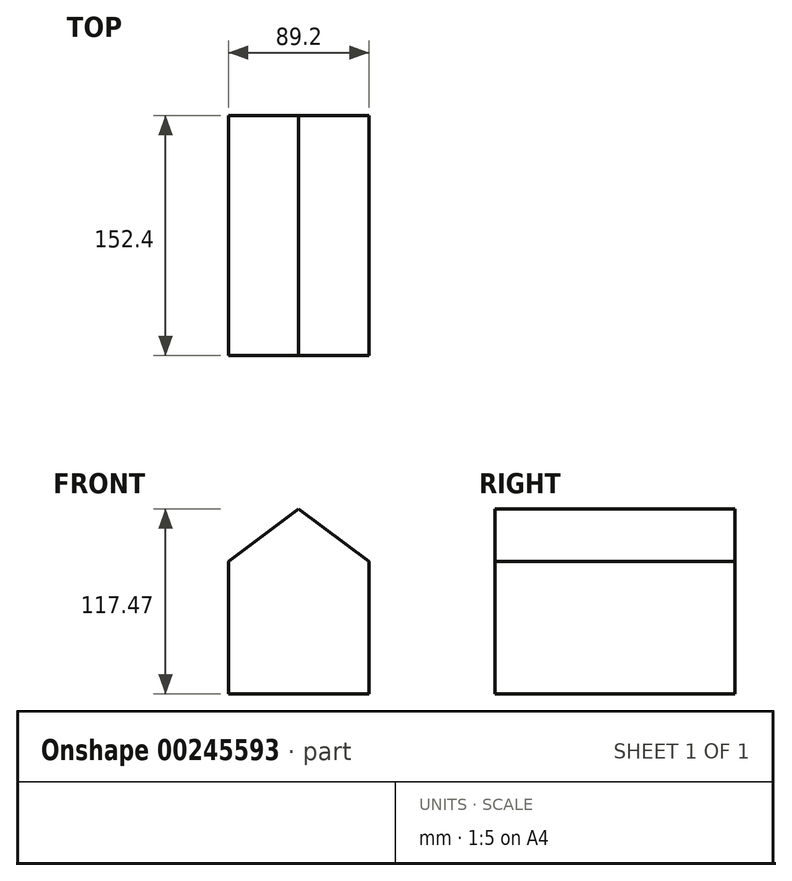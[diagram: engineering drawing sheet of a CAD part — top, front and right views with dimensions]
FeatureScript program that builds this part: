
annotation { "Feature Type Name" : "Feature", "Feature Type Description" : "" }
export const myFeature = defineFeature(function(context is Context, id is Id, definition is map)
    precondition{}
    {
        {
            var Q0;
            Q0=qCreatedBy(makeId("Front.planeOp"),FACE);
            var sketch = newSketch(context, id + "F0", { "sketchPlane" : qUnion([Q0])});
            skLineSegment(sketch, "E0.bottom", {"start": v(-44.6, 42.12) * mm, "end": v(44.6, 42.12) * mm});
            skLineSegment(sketch, "E0.top", {"start": v(-44.6, -42.12) * mm, "end": v(44.6, -42.12) * mm});
            skLineSegment(sketch, "E0.left", {"start": v(-44.6, 42.12) * mm, "end": v(-44.6, -42.12) * mm});
            skLineSegment(sketch, "E0.right", {"start": v(44.6, 42.12) * mm, "end": v(44.6, -42.12) * mm});
            skPoint(sketch, "E0.middle", {"position": v(0, 0) * mm});
            skLineSegment(sketch, "E1", {"start": v(0, 75.35) * mm, "end": v(-44.6, 42.12) * mm});
            skLineSegment(sketch, "E2", {"start": v(0, 75.35) * mm, "end": v(44.6, 42.12) * mm});
            skSolve(sketch);
        }
        {
            var Q0;
            Q0=makeQuery(id+"F0.imprint","IMPRINT",FACE,{"disambiguationData":[TD([[makeQuery(id+"F0.imprint","IMPRINT",EDGE,{"derivedFrom":sQuery(id+"F0.wireOp",EDGE,"E0.bottom")}),1.0]])]});
            var Q1;
            Q1=makeQuery(id+"F0.imprint","IMPRINT",FACE,{"disambiguationData":[TD([[makeQuery(id+"F0.imprint","IMPRINT",EDGE,{"derivedFrom":sQuery(id+"F0.wireOp",EDGE,"E0.bottom")}),-1.0]])]});
            extrude(context, id + "F1", {"entities" : qUnion([Q0, Q1]), "endBound" : BoundingType.SYMMETRIC, "depth" : 152.4 * mm});
        }
    });
